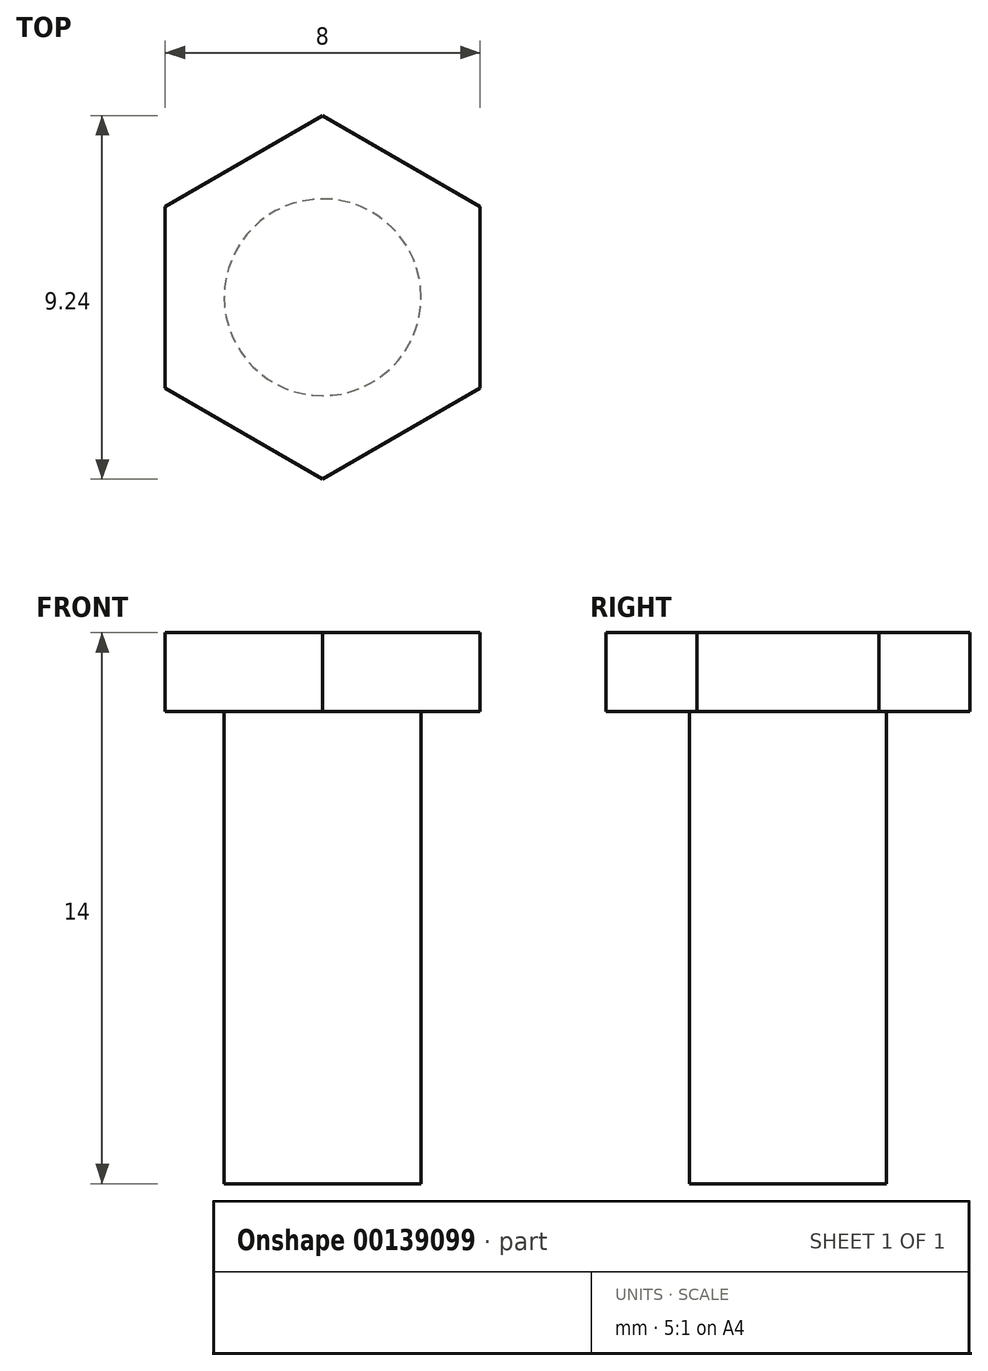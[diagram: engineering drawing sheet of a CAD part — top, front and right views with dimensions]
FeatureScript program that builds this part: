
annotation { "Feature Type Name" : "Feature", "Feature Type Description" : "" }
export const myFeature = defineFeature(function(context is Context, id is Id, definition is map)
    precondition{}
    {
        {
            var Q0;
            Q0=qCreatedBy(makeId("Top.planeOp"),FACE);
            var sketch = newSketch(context, id + "F0", { "sketchPlane" : qUnion([Q0])});
            skCircle(sketch, "E0", {"center": v(0, 0) * mm, "radius": 2.5 * mm});
            skSolve(sketch);
        }
        {
            var Q0;
            Q0=makeQuery(id+"F0.imprint","IMPRINT",FACE,{"disambiguationData":[TD([[makeQuery(id+"F0.imprint","IMPRINT",EDGE,{"derivedFrom":sQuery(id+"F0.wireOp",EDGE,"E0")}),1.0]])]});
            extrude(context, id + "F1", {"entities" : qUnion([Q0]), "depth" : 12 * mm});
        }
        {
            var Q0;
            Q0=makeQuery(id+"F1.opExtrude","CAP_FACE",FACE,{"disambiguationData":[OSD([sQuery(id+"F0.wireOp",EDGE,"E0")])],"isStart":false});
            var sketch = newSketch(context, id + "F2", { "sketchPlane" : qUnion([Q0])});
            skCircle(sketch, "E1.cCircle", {"center": v(0, 0) * mm, "radius": 4 * mm, "construction": true});
            skLineSegment(sketch, "E1.0", {"start": v(-4, -2.3) * mm, "end": v(-4, 2.3) * mm});
            skLineSegment(sketch, "E1.1", {"start": v(-4, 2.3) * mm, "end": v(0, 4.62) * mm});
            skLineSegment(sketch, "E1.2", {"start": v(0, 4.62) * mm, "end": v(4, 2.3) * mm});
            skLineSegment(sketch, "E1.3", {"start": v(4, 2.3) * mm, "end": v(4, -2.3) * mm});
            skLineSegment(sketch, "E1.4", {"start": v(4, -2.3) * mm, "end": v(0, -4.62) * mm});
            skLineSegment(sketch, "E1.5", {"start": v(0, -4.62) * mm, "end": v(-4, -2.3) * mm});
            skPoint(sketch, "E1.0.midPoint", {"position": v(-4, 0) * mm});
            skSolve(sketch);
        }
        {
            var Q0;
            Q0 = qSketchRegion(id + "F2", true);
            extrude(context, id + "F3", {"entities" : qUnion([Q0]), "operationType" : NewBodyOperationType.ADD, "depth" : 2 * mm});
        }
    });
